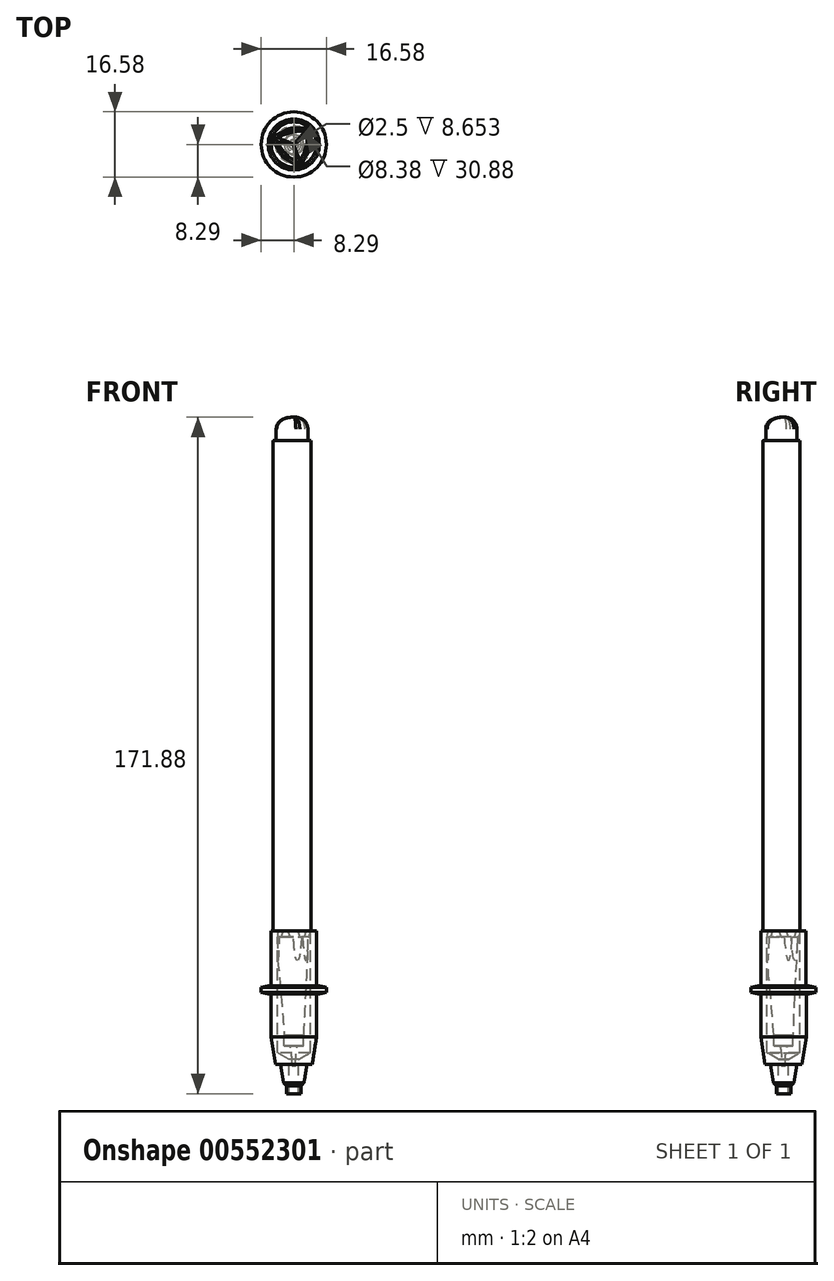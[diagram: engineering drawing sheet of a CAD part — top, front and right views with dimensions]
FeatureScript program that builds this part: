
annotation { "Feature Type Name" : "Feature", "Feature Type Description" : "" }
export const myFeature = defineFeature(function(context is Context, id is Id, definition is map)
    precondition{}
    {
        {
            var Q0;
            Q0=qCreatedBy(makeId("Front.planeOp"),FACE);
            var sketch = newSketch(context, id + "F0", { "sketchPlane" : qUnion([Q0])});
            skLineSegment(sketch, "E0", {"start": v(0, 0) * mm, "end": v(5.74, 0) * mm});
            skLineSegment(sketch, "E1", {"start": v(5.74, 0) * mm, "end": v(5.74, -13.93) * mm});
            skLineSegment(sketch, "E2", {"start": v(5.74, -13.93) * mm, "end": v(8.29, -13.93) * mm});
            skLineSegment(sketch, "E3", {"start": v(8.29, -13.93) * mm, "end": v(8.29, -15.93) * mm});
            skLineSegment(sketch, "E4", {"start": v(8.29, -15.93) * mm, "end": v(5.79, -15.93) * mm});
            skLineSegment(sketch, "E5", {"start": v(5.8, -15.93) * mm, "end": v(5.8, -26.88) * mm});
            skLineSegment(sketch, "E6", {"start": v(5.79, -26.88) * mm, "end": v(4.68, -33.8) * mm});
            skLineSegment(sketch, "E7", {"start": v(4.68, -33.8) * mm, "end": v(3.37, -33.8) * mm});
            skLineSegment(sketch, "E8", {"start": v(3.37, -33.8) * mm, "end": v(2.59, -38.5) * mm});
            skLineSegment(sketch, "E9", {"start": v(2.59, -38.5) * mm, "end": v(1.82, -39.38) * mm});
            skLineSegment(sketch, "E10", {"start": v(1.82, -39.38) * mm, "end": v(1.82, -41.3) * mm});
            skLineSegment(sketch, "E11", {"start": v(1.82, -41.3) * mm, "end": v(0, -41.3) * mm});
            skLineSegment(sketch, "E12", {"start": v(0, 0) * mm, "end": v(0, -41.3) * mm});
            skLineSegment(sketch, "E13", {"start": v(5.79, -15.93) * mm, "end": v(13.42, -15.93) * mm, "construction": true});
            skLineSegment(sketch, "E14", {"start": v(5.74, -13.93) * mm, "end": v(13.47, -13.93) * mm, "construction": true});
            skSolve(sketch);
        }
        {
            var Q0;
            Q0 = qSketchRegion(id + "F0", true);
            var Q1;
            Q1=sQuery(id+"F0.wireOp",EDGE,"E12");
            revolve(context, id + "F1", {"entities" : qUnion([Q0]), "axis" : qUnion([Q1]), "revolveType" : RevolveType.FULL});
        }
        {
            var Q0;
            Q0=makeQuery(id+"F1.opRevolve","SWEPT_FACE",FACE,{"disambiguationData":[OSD([sQuery(id+"F0.wireOp",EDGE,"E0")])]});
            var sketch = newSketch(context, id + "F2", { "sketchPlane" : qUnion([Q0])});
            skPoint(sketch, "E15", {"position": v(0, 0) * mm});
            skSolve(sketch);
        }
        {
            var Q0;
            Q0=sQuery(id+"F2.wireOp",VERTEX,"E15");
            var Q1;
            Q1=makeQuery(id+"F1.opRevolve","SWEPT_BODY",BODY,{"disambiguationData":[OSD([sQuery(id+"F0.wireOp",EDGE,"E0"),sQuery(id+"F0.wireOp",EDGE,"E1"),sQuery(id+"F0.wireOp",EDGE,"E2"),sQuery(id+"F0.wireOp",EDGE,"E3"),sQuery(id+"F0.wireOp",EDGE,"E4"),sQuery(id+"F0.wireOp",EDGE,"E5"),sQuery(id+"F0.wireOp",EDGE,"E6"),sQuery(id+"F0.wireOp",EDGE,"E7"),sQuery(id+"F0.wireOp",EDGE,"E8"),sQuery(id+"F0.wireOp",EDGE,"E9"),sQuery(id+"F0.wireOp",EDGE,"E10"),sQuery(id+"F0.wireOp",EDGE,"E11"),sQuery(id+"F0.wireOp",EDGE,"E12")])]});
            hole(context, id + "F3", {"style" : HoleStyle.SIMPLE, "endStyle" : HoleEndStyle.THROUGH, "holeDiameter" : 2.5 * mm, "isTappedThrough" : true, "tappedDepth" : 12 * mm, "tapClearance" : 3, "locations" : qUnion([Q0]), "scope" : qUnion([Q1])});
        }
        {
            var Q0;
            Q0=sQuery(id+"F2.wireOp",VERTEX,"E15");
            var Q1;
            Q1=makeQuery(id+"F1.opRevolve","SWEPT_BODY",BODY,{"disambiguationData":[OSD([sQuery(id+"F0.wireOp",EDGE,"E0"),sQuery(id+"F0.wireOp",EDGE,"E1"),sQuery(id+"F0.wireOp",EDGE,"E2"),sQuery(id+"F0.wireOp",EDGE,"E3"),sQuery(id+"F0.wireOp",EDGE,"E4"),sQuery(id+"F0.wireOp",EDGE,"E5"),sQuery(id+"F0.wireOp",EDGE,"E6"),sQuery(id+"F0.wireOp",EDGE,"E7"),sQuery(id+"F0.wireOp",EDGE,"E8"),sQuery(id+"F0.wireOp",EDGE,"E9"),sQuery(id+"F0.wireOp",EDGE,"E10"),sQuery(id+"F0.wireOp",EDGE,"E11"),sQuery(id+"F0.wireOp",EDGE,"E12")])]});
            hole(context, id + "F4", {"style" : HoleStyle.SIMPLE, "endStyle" : HoleEndStyle.BLIND, "holeDiameter" : 8.38 * mm, "holeDepth" : 30.88 * mm, "isTappedThrough" : true, "tappedDepth" : 12 * mm, "tapClearance" : 3, "locations" : qUnion([Q0]), "scope" : qUnion([Q1])});
        }
        {
            var Q0;
            Q0=makeQuery(id+"F1.opRevolve","SWEPT_EDGE",EDGE,{"disambiguationData":[OSD([sQuery(id+"F0.wireOp",EDGE,"E2"),sQuery(id+"F0.wireOp",EDGE,"E3")])]});
            var Q1;
            Q1=makeQuery(id+"F1.opRevolve","SWEPT_EDGE",EDGE,{"disambiguationData":[OSD([sQuery(id+"F0.wireOp",EDGE,"E3"),sQuery(id+"F0.wireOp",EDGE,"E4")])]});
            chamfer(context, id + "F5", {"entities" : qUnion([Q0, Q1]), "chamferType" : ChamferType.OFFSET_ANGLE, "width" : 1.8 * mm, "oppositeDirection" : false, "angle" : 12 * degree, "tangentPropagation" : true});
        }
        {
            var Q0;
            Q0=qCreatedBy(makeId("Top.planeOp"),FACE);
            var sketch = newSketch(context, id + "F6", { "sketchPlane" : qUnion([Q0])});
            skCircle(sketch, "E16.cCircle", {"center": v(0, 0) * mm, "radius": 5.93 * mm, "construction": true});
            skLineSegment(sketch, "E16.0", {"start": v(4.31, 4.07) * mm, "end": v(1.37, -5.77) * mm, "construction": true});
            skLineSegment(sketch, "E16.1", {"start": v(1.37, -5.77) * mm, "end": v(-5.68, 1.7) * mm, "construction": true});
            skLineSegment(sketch, "E16.2", {"start": v(-5.68, 1.7) * mm, "end": v(4.31, 4.07) * mm, "construction": true});
            skArc(sketch, "E17", {"start": v(2.86, 4.17) * mm, "mid": v(-0.9, 3.77) * mm, "end": v(-4.43, 2.44) * mm});
            skArc(sketch, "E18", {"start": v(2.18, -4.56) * mm, "mid": v(3.7, -1.1) * mm, "end": v(4.33, 2.61) * mm});
            skArc(sketch, "E19", {"start": v(-5.04, 0.39) * mm, "mid": v(-2.81, -2.66) * mm, "end": v(0.1, -5.05) * mm});
            skPoint(sketch, "E20.visualSharp", {"position": v(4.31, 4.07) * mm});
            skArc(sketch, "E20.filletArc", {"start": v(4.33, 2.61) * mm, "mid": v(3.92, 3.7) * mm, "end": v(2.86, 4.17) * mm});
            skPoint(sketch, "E21.visualSharp", {"position": v(1.37, -5.77) * mm});
            skArc(sketch, "E21.filletArc", {"start": v(0.1, -5.05) * mm, "mid": v(1.25, -5.24) * mm, "end": v(2.18, -4.56) * mm});
            skPoint(sketch, "E22.visualSharp", {"position": v(-5.68, 1.7) * mm});
            skArc(sketch, "E22.filletArc", {"start": v(-4.43, 2.44) * mm, "mid": v(-5.16, 1.54) * mm, "end": v(-5.04, 0.39) * mm});
            skSolve(sketch);
        }
        {
            var Q0;
            Q0 = qSketchRegion(id + "F6", true);
            extrude(context, id + "F7", {"entities" : qUnion([Q0]), "depth" : 124.58 * mm, "offsetDistance" : 25 * mm});
        }
        {
            var Q0;
            Q0=makeQuery(id+"F7.opExtrude","CAP_FACE",FACE,{"disambiguationData":[OSD([sQuery(id+"F6.wireOp",EDGE,"E17"),sQuery(id+"F6.wireOp",EDGE,"E18"),sQuery(id+"F6.wireOp",EDGE,"E19"),sQuery(id+"F6.wireOp",EDGE,"E20.filletArc"),sQuery(id+"F6.wireOp",EDGE,"E21.filletArc"),sQuery(id+"F6.wireOp",EDGE,"E22.filletArc")])],"isStart":false});
            var sketch = newSketch(context, id + "F8", { "sketchPlane" : qUnion([Q0])});
            skArc(sketch, "E23.0", {"start": v(2.86, 4.17) * mm, "mid": v(-0.9, 3.77) * mm, "end": v(-4.43, 2.44) * mm});
            skArc(sketch, "E23.1", {"start": v(4.33, 2.61) * mm, "mid": v(3.92, 3.7) * mm, "end": v(2.86, 4.17) * mm});
            skArc(sketch, "E23.2", {"start": v(2.18, -4.56) * mm, "mid": v(3.7, -1.1) * mm, "end": v(4.33, 2.61) * mm});
            skArc(sketch, "E23.3", {"start": v(0.1, -5.05) * mm, "mid": v(1.25, -5.24) * mm, "end": v(2.18, -4.56) * mm});
            skArc(sketch, "E23.4", {"start": v(-5.04, 0.39) * mm, "mid": v(-2.81, -2.66) * mm, "end": v(0.1, -5.05) * mm});
            skArc(sketch, "E23.5", {"start": v(-4.43, 2.44) * mm, "mid": v(-5.16, 1.54) * mm, "end": v(-5.04, 0.39) * mm});
            skPoint(sketch, "E23.6", {"position": v(3.92, 3.7) * mm});
            skArc(sketch, "E24.0", {"start": v(-4.07, 1.77) * mm, "mid": v(-4.44, 1.32) * mm, "end": v(-4.37, 0.76) * mm});
            skArc(sketch, "E24.1", {"start": v(0.5, -4.41) * mm, "mid": v(1.07, -4.5) * mm, "end": v(1.53, -4.17) * mm});
            skArc(sketch, "E24.2", {"start": v(1.53, -4.17) * mm, "mid": v(2.98, -0.9) * mm, "end": v(3.57, 2.64) * mm});
            skArc(sketch, "E24.3", {"start": v(-4.37, 0.76) * mm, "mid": v(-2.26, -2.14) * mm, "end": v(0.5, -4.41) * mm});
            skArc(sketch, "E24.4", {"start": v(3.57, 2.64) * mm, "mid": v(3.37, 3.18) * mm, "end": v(2.84, 3.41) * mm});
            skArc(sketch, "E24.5", {"start": v(2.84, 3.41) * mm, "mid": v(-0.72, 3.03) * mm, "end": v(-4.07, 1.77) * mm});
            skSolve(sketch);
        }
        {
            var Q0;
            Q0=makeQuery(id+"F8.imprint","IMPRINT",FACE,{"disambiguationData":[TD([[makeQuery(id+"F8.imprint","IMPRINT",EDGE,{"derivedFrom":sQuery(id+"F8.wireOp",EDGE,"E24.0")}),1.0]])]});
            extrude(context, id + "F9", {"entities" : qUnion([Q0]), "operationType" : NewBodyOperationType.ADD, "depth" : 6 * mm, "offsetDistance" : 25 * mm});
        }
        {
            var Q0;
            Q0=makeQuery(id+"F9.opExtrude","CAP_EDGE",EDGE,{"disambiguationData":[OSD([sQuery(id+"F8.wireOp",EDGE,"E24.3")])],"isStart":false});
            fillet(context, id + "F10", {"entities" : qUnion([Q0]), "radius" : 3 * mm, "tangentPropagation" : true, "allowEdgeOverflow" : false});
        }
        {
            var Q0;
            Q0=makeQuery(id+"F7.opExtrude","CAP_FACE",FACE,{"disambiguationData":[OSD([sQuery(id+"F6.wireOp",EDGE,"E17"),sQuery(id+"F6.wireOp",EDGE,"E18"),sQuery(id+"F6.wireOp",EDGE,"E19"),sQuery(id+"F6.wireOp",EDGE,"E20.filletArc"),sQuery(id+"F6.wireOp",EDGE,"E21.filletArc"),sQuery(id+"F6.wireOp",EDGE,"E22.filletArc")])],"isStart":true});
            cPlane(context, id + "F11", {"entities" : qUnion([Q0]), "cplaneType" : CPlaneType.OFFSET, "offset" : 1.43 * mm, "width" : 150 * mm, "height" : 150 * mm});
        }
        {
            var Q0;
            Q0=qCreatedBy(id+"F11.planeOp",FACE);
            var sketch = newSketch(context, id + "F12", { "sketchPlane" : qUnion([Q0])});
            skArc(sketch, "E25.0.0", {"start": v(0.1, 5.05) * mm, "mid": v(-2.81, 2.66) * mm, "end": v(-5.04, -0.39) * mm});
            skArc(sketch, "E25.0.1", {"start": v(-5.04, -0.39) * mm, "mid": v(-5.16, -1.54) * mm, "end": v(-4.43, -2.44) * mm});
            skArc(sketch, "E25.0.2", {"start": v(-4.43, -2.44) * mm, "mid": v(-0.9, -3.77) * mm, "end": v(2.86, -4.17) * mm});
            skArc(sketch, "E25.0.3", {"start": v(2.86, -4.17) * mm, "mid": v(3.92, -3.7) * mm, "end": v(4.33, -2.61) * mm});
            skArc(sketch, "E25.0.4", {"start": v(4.33, -2.61) * mm, "mid": v(3.7, 1.1) * mm, "end": v(2.18, 4.56) * mm});
            skArc(sketch, "E25.0.5", {"start": v(2.18, 4.56) * mm, "mid": v(1.25, 5.24) * mm, "end": v(0.1, 5.05) * mm});
            skArc(sketch, "E26.0", {"start": v(1.67, 4.25) * mm, "mid": v(1.1, 4.66) * mm, "end": v(0.42, 4.55) * mm});
            skArc(sketch, "E26.1", {"start": v(-4.51, -0.68) * mm, "mid": v(-4.59, -1.37) * mm, "end": v(-4.15, -1.9) * mm});
            skArc(sketch, "E26.2", {"start": v(-4.15, -1.9) * mm, "mid": v(-0.76, -3.18) * mm, "end": v(2.84, -3.57) * mm});
            skArc(sketch, "E26.3", {"start": v(0.42, 4.55) * mm, "mid": v(-2.38, 2.25) * mm, "end": v(-4.51, -0.68) * mm});
            skArc(sketch, "E26.4", {"start": v(2.84, -3.57) * mm, "mid": v(3.48, -3.29) * mm, "end": v(3.73, -2.64) * mm});
            skArc(sketch, "E26.5", {"start": v(3.73, -2.64) * mm, "mid": v(3.13, 0.94) * mm, "end": v(1.67, 4.25) * mm});
            skArc(sketch, "E27.0", {"start": v(4.12, -2.62) * mm, "mid": v(3.5, 1.05) * mm, "end": v(2, 4.45) * mm});
            skArc(sketch, "E27.1", {"start": v(0.21, 4.88) * mm, "mid": v(-2.66, 2.51) * mm, "end": v(-4.86, -0.49) * mm});
            skArc(sketch, "E27.2", {"start": v(-4.86, -0.49) * mm, "mid": v(-4.96, -1.48) * mm, "end": v(-4.33, -2.25) * mm});
            skArc(sketch, "E27.3", {"start": v(2, 4.45) * mm, "mid": v(1.2, 5.04) * mm, "end": v(0.21, 4.88) * mm});
            skArc(sketch, "E27.4", {"start": v(-4.33, -2.25) * mm, "mid": v(-0.85, -3.56) * mm, "end": v(2.85, -3.96) * mm});
            skArc(sketch, "E27.5", {"start": v(2.85, -3.96) * mm, "mid": v(3.76, -3.56) * mm, "end": v(4.12, -2.62) * mm});
            skSolve(sketch);
        }
        {
            var Q0;
            Q0=qCreatedBy(id+"F11.planeOp",FACE);
            var sketch = newSketch(context, id + "F13", { "sketchPlane" : qUnion([Q0])});
            skArc(sketch, "E28.0.0", {"start": v(0.1, 5.05) * mm, "mid": v(-2.81, 2.66) * mm, "end": v(-5.04, -0.39) * mm});
            skArc(sketch, "E28.0.1", {"start": v(-5.04, -0.39) * mm, "mid": v(-5.16, -1.54) * mm, "end": v(-4.43, -2.44) * mm});
            skArc(sketch, "E28.0.2", {"start": v(-4.43, -2.44) * mm, "mid": v(-0.9, -3.77) * mm, "end": v(2.86, -4.17) * mm});
            skArc(sketch, "E28.0.3", {"start": v(2.86, -4.17) * mm, "mid": v(3.92, -3.7) * mm, "end": v(4.33, -2.61) * mm});
            skArc(sketch, "E28.0.4", {"start": v(4.33, -2.61) * mm, "mid": v(3.7, 1.1) * mm, "end": v(2.18, 4.56) * mm});
            skArc(sketch, "E28.0.5", {"start": v(2.18, 4.56) * mm, "mid": v(1.25, 5.24) * mm, "end": v(0.1, 5.05) * mm});
            skArc(sketch, "E29.0", {"start": v(4.12, -2.62) * mm, "mid": v(3.5, 1.05) * mm, "end": v(2, 4.45) * mm});
            skArc(sketch, "E29.1", {"start": v(0.21, 4.88) * mm, "mid": v(-2.66, 2.51) * mm, "end": v(-4.86, -0.49) * mm});
            skArc(sketch, "E29.2", {"start": v(-4.86, -0.49) * mm, "mid": v(-4.96, -1.48) * mm, "end": v(-4.33, -2.25) * mm});
            skArc(sketch, "E29.3", {"start": v(2, 4.45) * mm, "mid": v(1.2, 5.04) * mm, "end": v(0.21, 4.88) * mm});
            skArc(sketch, "E29.4", {"start": v(-4.33, -2.25) * mm, "mid": v(-0.85, -3.56) * mm, "end": v(2.85, -3.96) * mm});
            skArc(sketch, "E29.5", {"start": v(2.85, -3.96) * mm, "mid": v(3.76, -3.56) * mm, "end": v(4.12, -2.62) * mm});
            skSolve(sketch);
        }
        {
            var Q1;
            Q1=makeQuery(id+"F7.opExtrude","CAP_FACE",FACE,{"disambiguationData":[OSD([sQuery(id+"F6.wireOp",EDGE,"E17"),sQuery(id+"F6.wireOp",EDGE,"E18"),sQuery(id+"F6.wireOp",EDGE,"E19"),sQuery(id+"F6.wireOp",EDGE,"E20.filletArc"),sQuery(id+"F6.wireOp",EDGE,"E21.filletArc"),sQuery(id+"F6.wireOp",EDGE,"E22.filletArc")])],"isStart":true});
            var Q2;
            Q2=makeQuery(id+"F13.imprint","IMPRINT",FACE,{"disambiguationData":[TD([[makeQuery(id+"F13.imprint","IMPRINT",EDGE,{"derivedFrom":sQuery(id+"F13.wireOp",EDGE,"E29.0")}),1.0]])]});
            loft(context, id + "F14", {"operationType" : NewBodyOperationType.ADD, "sheetProfilesArray" : [{ "sheetProfileEntities" : qUnion([Q1]) }, { "sheetProfileEntities" : qUnion([Q2]) }]});
        }
        {
            var Q0;
            Q0=makeQuery(id+"F12.imprint","IMPRINT",FACE,{"disambiguationData":[TD([[makeQuery(id+"F12.imprint","IMPRINT",EDGE,{"derivedFrom":sQuery(id+"F12.wireOp",EDGE,"E26.0")}),1.0]])]});
            cPlane(context, id + "F15", {"entities" : qUnion([Q0]), "cplaneType" : CPlaneType.OFFSET, "offset" : 25 * mm, "width" : 150 * mm, "height" : 150 * mm});
        }
        {
            var Q0;
            Q0=qCreatedBy(id+"F15.planeOp",FACE);
            var sketch = newSketch(context, id + "F16", { "sketchPlane" : qUnion([Q0])});
            skPoint(sketch, "E30.0", {"position": v(0, 0) * mm});
            skCircle(sketch, "E31", {"center": v(0, 0) * mm, "radius": 2.43 * mm});
            skSolve(sketch);
        }
        {
            var Q1;
            Q1=makeQuery(id+"F12.imprint","IMPRINT",FACE,{"disambiguationData":[TD([[makeQuery(id+"F12.imprint","IMPRINT",EDGE,{"derivedFrom":sQuery(id+"F12.wireOp",EDGE,"E26.0")}),1.0]])]});
            var Q2;
            Q2=makeQuery(id+"F16.imprint","IMPRINT",FACE,{"disambiguationData":[TD([[makeQuery(id+"F16.imprint","IMPRINT",EDGE,{"derivedFrom":sQuery(id+"F16.wireOp",EDGE,"E31")}),1.0]])]});
            loft(context, id + "F17", {"operationType" : NewBodyOperationType.ADD, "sheetProfilesArray" : [{ "sheetProfileEntities" : qUnion([Q1]) }, { "sheetProfileEntities" : qUnion([Q2]) }]});
        }
        {
            var Q0;
            Q0=makeQuery(id+"F17.opLoft","CAP_FACE",FACE,{"disambiguationData":[OSD([makeQuery(id+"F16.imprint","IMPRINT",FACE,{"disambiguationData":[TD([[makeQuery(id+"F16.imprint","IMPRINT",EDGE,{"derivedFrom":sQuery(id+"F16.wireOp",EDGE,"E31")}),1.0]])]})])],"isStart":true});
            extrude(context, id + "F18", {"entities" : qUnion([Q0]), "operationType" : NewBodyOperationType.ADD, "depth" : 2.75 * mm, "offsetDistance" : 25 * mm});
        }
        {
            var Q0;
            Q0=makeQuery(id+"F18.opExtrude","CAP_FACE",FACE,{"disambiguationData":[OSD([makeQuery(id+"F16.imprint","IMPRINT",FACE,{"disambiguationData":[TD([[makeQuery(id+"F16.imprint","IMPRINT",EDGE,{"derivedFrom":sQuery(id+"F16.wireOp",EDGE,"E31")}),1.0]])]})])],"isStart":false});
            var sketch = newSketch(context, id + "F19", { "sketchPlane" : qUnion([Q0])});
            skCircle(sketch, "E32", {"center": v(0, 0) * mm, "radius": 1.15 * mm});
            skSolve(sketch);
        }
        {
            var Q0;
            Q0=makeQuery(id+"F19.imprint","IMPRINT",FACE,{"disambiguationData":[TD([[makeQuery(id+"F19.imprint","IMPRINT",EDGE,{"derivedFrom":sQuery(id+"F19.wireOp",EDGE,"E32")}),-1.0]])]});
            cPlane(context, id + "F20", {"entities" : qUnion([Q0]), "cplaneType" : CPlaneType.OFFSET, "offset" : 5 * mm, "width" : 150 * mm, "height" : 150 * mm});
        }
        {
            var Q0;
            Q0=qCreatedBy(id+"F20.planeOp",FACE);
            var sketch = newSketch(context, id + "F21", { "sketchPlane" : qUnion([Q0])});
            skCircle(sketch, "E33", {"center": v(0, 0) * mm, "radius": 0.5 * mm});
            skSolve(sketch);
        }
        {
            var Q0;
            Q0=qCreatedBy(makeId("Front.planeOp"),FACE);
            var sketch = newSketch(context, id + "F22", { "sketchPlane" : qUnion([Q0])});
            skLineSegment(sketch, "E34.0.0", {"start": v(1.15, -29.18) * mm, "end": v(-1.15, -29.18) * mm});
            skLineSegment(sketch, "E35.0", {"start": v(0.5, -34.18) * mm, "end": v(-0.5, -34.18) * mm});
            skFitSpline(sketch, "E36", {"points": [v(0.5, -34.18) * mm, v(1.15, -29.18) * mm], "startDerivative": vector(0.04, 3.57) * mm, "endDerivative": vector(2.29, 0.71) * mm});
            skLineSegment(sketch, "E37", {"start": v(0, -34.18) * mm, "end": v(0, -29.18) * mm});
            skSolve(sketch);
        }
        {
            var Q0;
            {var subQ0=sQuery(id+"F22.wireOp",EDGE,"E36");Q0=makeQuery(id+"F22.imprint","IMPRINT",FACE,{"disambiguationData":[TD([[makeQuery(id+"F22.imprint","IMPRINT",EDGE,{"derivedFrom":subQ0}),1.0]])]});}
            var Q1;
            Q1=sQuery(id+"F22.wireOp",EDGE,"E37");
            revolve(context, id + "F23", {"operationType" : NewBodyOperationType.ADD, "entities" : qUnion([Q0]), "axis" : qUnion([Q1]), "revolveType" : RevolveType.FULL});
        }
    });
